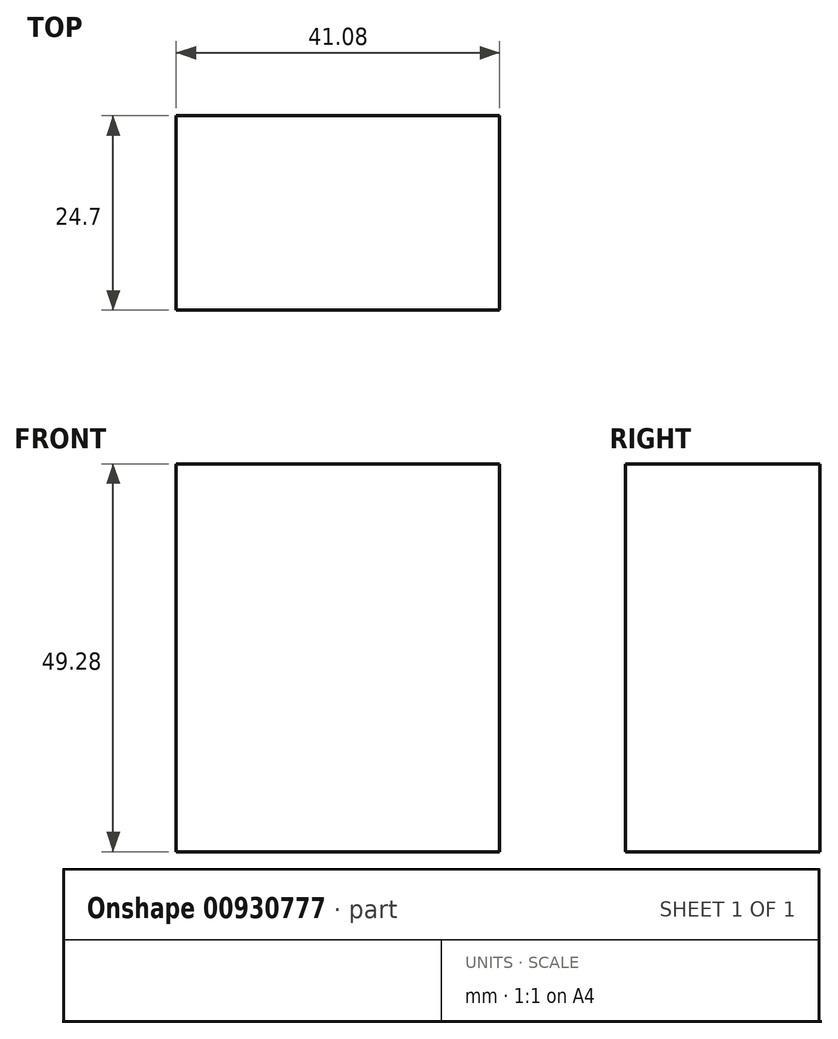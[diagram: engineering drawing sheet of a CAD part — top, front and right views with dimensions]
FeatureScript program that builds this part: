
annotation { "Feature Type Name" : "Feature", "Feature Type Description" : "" }
export const myFeature = defineFeature(function(context is Context, id is Id, definition is map)
    precondition{}
    {
        {
            var Q0;
            Q0=qCreatedBy(makeId("Top.planeOp"),FACE);
            var sketch = newSketch(context, id + "F0", { "sketchPlane" : qUnion([Q0])});
            skLineSegment(sketch, "E0", {"start": v(-59.24, -51.21) * mm, "end": v(34.95, 7.75) * mm});
            skLineSegment(sketch, "E1.bottom", {"start": v(7.23, -33.77) * mm, "end": v(48.31, -33.77) * mm});
            skLineSegment(sketch, "E1.top", {"start": v(7.23, -58.47) * mm, "end": v(48.31, -58.47) * mm});
            skLineSegment(sketch, "E1.left", {"start": v(7.23, -33.77) * mm, "end": v(7.23, -58.47) * mm});
            skLineSegment(sketch, "E1.right", {"start": v(48.31, -33.77) * mm, "end": v(48.31, -58.47) * mm});
            skSolve(sketch);
        }
        {
            var Q0;
            Q0=makeQuery(id+"F0.imprint","IMPRINT",FACE,{"disambiguationData":[TD([[makeQuery(id+"F0.imprint","IMPRINT",EDGE,{"derivedFrom":sQuery(id+"F0.wireOp",EDGE,"E1.bottom")}),-1.0]])]});
            extrude(context, id + "F1", {"entities" : qUnion([Q0]), "depth" : 49.28 * mm, "offsetDistance" : 25.4 * mm});
        }
    });
